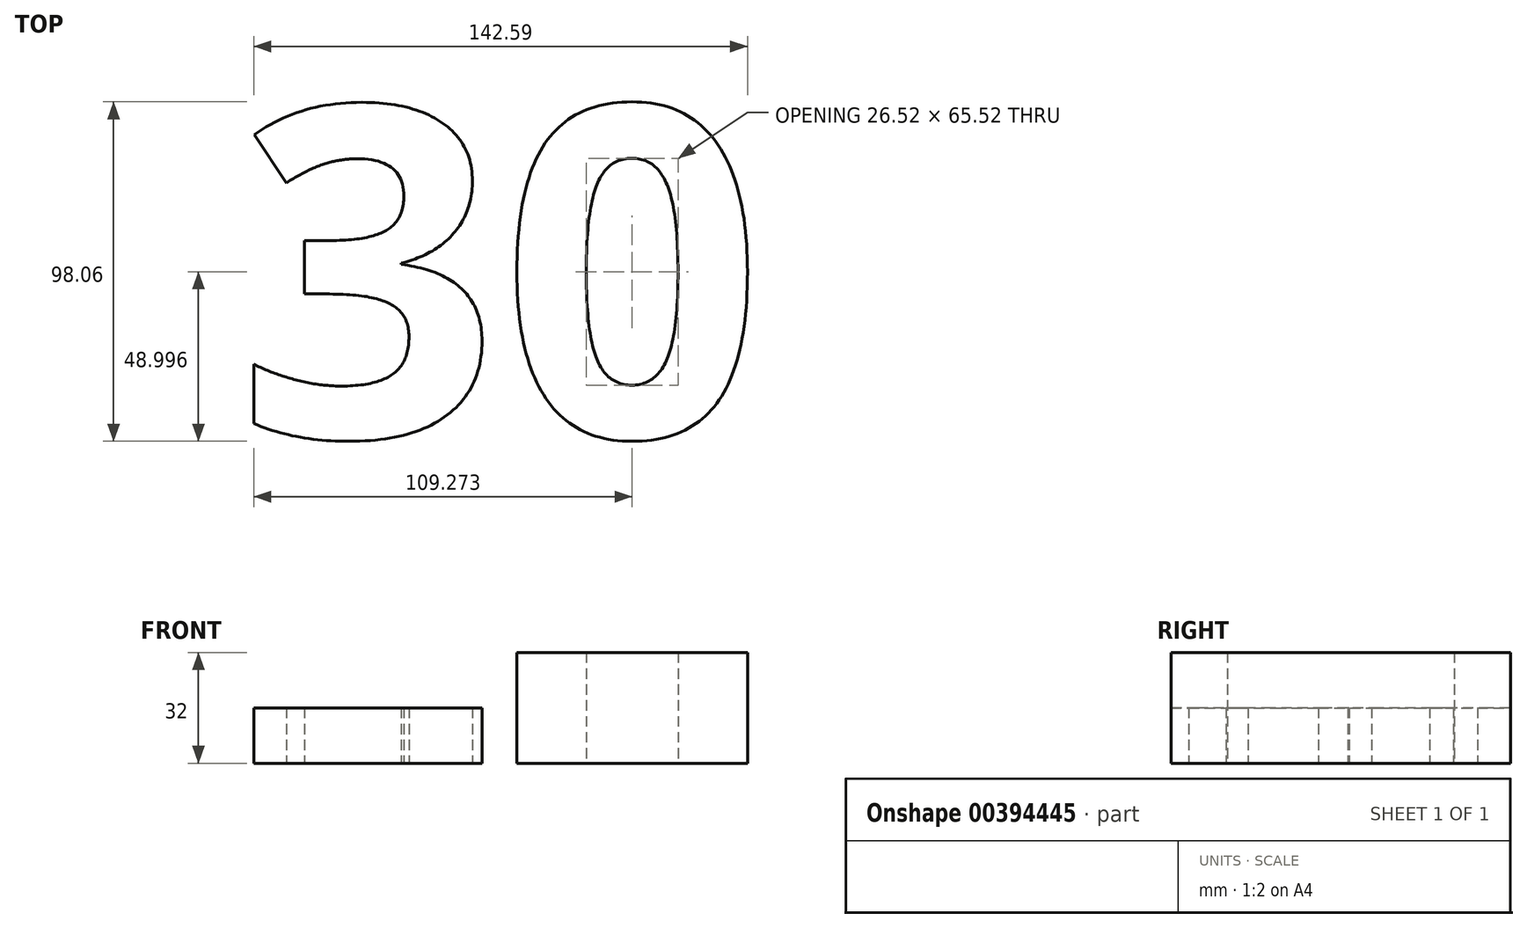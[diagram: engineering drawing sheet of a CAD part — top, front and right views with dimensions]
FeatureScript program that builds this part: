
annotation { "Feature Type Name" : "Feature", "Feature Type Description" : "" }
export const myFeature = defineFeature(function(context is Context, id is Id, definition is map)
    precondition{}
    {
        {
            var Q0;
            Q0=qCreatedBy(makeId("Top.planeOp"),FACE);
            var sketch = newSketch(context, id + "F0", { "sketchPlane" : qUnion([Q0])});
            skText(sketch, "E0", { "text": "30", "fontName": "NotoSans-Bold.ttf"});
            const initialGuessF0  = {"E0": [-0.05774, -0.01107, 1, 0, 0.09606]};
            skSetInitialGuess(sketch, initialGuessF0);
            skSolve(sketch);
        }
        {
            var Q0;
            Q0=makeQuery(id+"F0.imprint","IMPRINT",FACE,{"disambiguationData":[TD([[makeQuery(id+"F0.imprint","IMPRINT",EDGE,{"derivedFrom":sQuery(id+"F0.wireOp",EDGE,"E0.sketch_text.stroke-27")}),-1.0]])]});
            var Q1;
            Q1=makeQuery(id+"F0.imprint","IMPRINT",FACE,{"disambiguationData":[TD([[makeQuery(id+"F0.imprint","IMPRINT",EDGE,{"derivedFrom":sQuery(id+"F0.wireOp",EDGE,"E0.sketch_text.stroke-0")}),-1.0]])]});
            extrude(context, id + "F1", {"entities" : qUnion([Q0, Q1]), "depth" : 16 * mm});
        }
        {
            var Q0;
            Q0=makeQuery(id+"F1.opExtrude","CAP_FACE",FACE,{"disambiguationData":[OSD([sQuery(id+"F0.wireOp",EDGE,"E0.sketch_text.stroke-27"),sQuery(id+"F0.wireOp",EDGE,"E0.sketch_text.stroke-28"),sQuery(id+"F0.wireOp",EDGE,"E0.sketch_text.stroke-29"),sQuery(id+"F0.wireOp",EDGE,"E0.sketch_text.stroke-30"),sQuery(id+"F0.wireOp",EDGE,"E0.sketch_text.stroke-31"),sQuery(id+"F0.wireOp",EDGE,"E0.sketch_text.stroke-32"),sQuery(id+"F0.wireOp",EDGE,"E0.sketch_text.stroke-33"),sQuery(id+"F0.wireOp",EDGE,"E0.sketch_text.stroke-34"),sQuery(id+"F0.wireOp",EDGE,"E0.sketch_text.stroke-35"),sQuery(id+"F0.wireOp",EDGE,"E0.sketch_text.stroke-36"),sQuery(id+"F0.wireOp",EDGE,"E0.sketch_text.stroke-37"),sQuery(id+"F0.wireOp",EDGE,"E0.sketch_text.stroke-38"),sQuery(id+"F0.wireOp",EDGE,"E0.sketch_text.stroke-39"),sQuery(id+"F0.wireOp",EDGE,"E0.sketch_text.stroke-40"),sQuery(id+"F0.wireOp",EDGE,"E0.sketch_text.stroke-41"),sQuery(id+"F0.wireOp",EDGE,"E0.sketch_text.stroke-42")])],"isStart":false});
            extrude(context, id + "F2", {"entities" : qUnion([Q0]), "operationType" : NewBodyOperationType.ADD, "depth" : 16 * mm});
        }
    });
